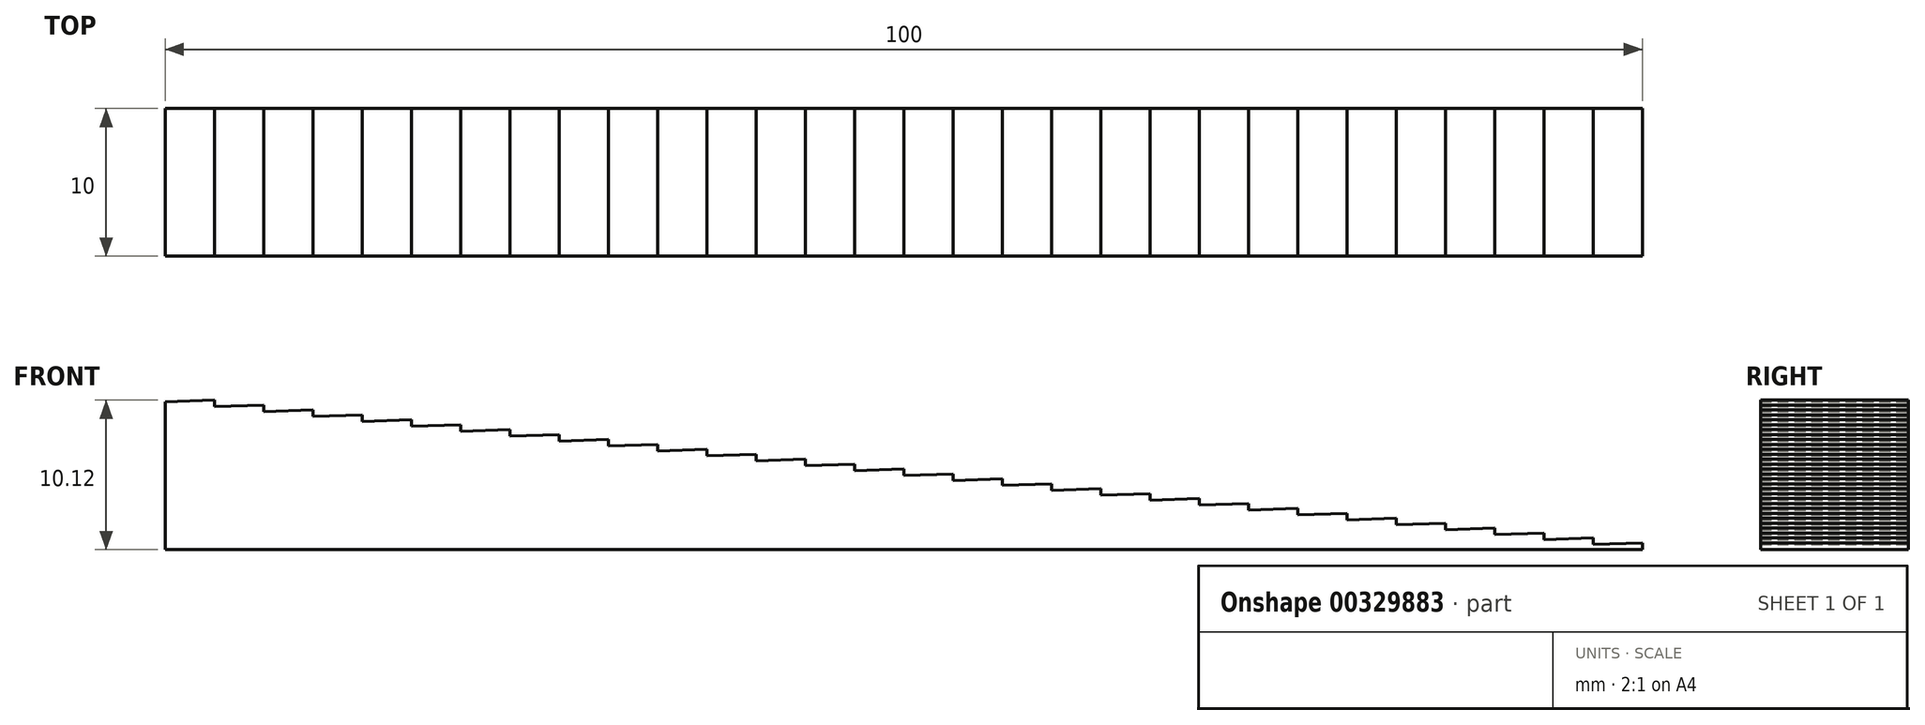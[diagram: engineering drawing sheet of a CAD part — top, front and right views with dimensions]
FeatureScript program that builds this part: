
annotation { "Feature Type Name" : "Feature", "Feature Type Description" : "" }
export const myFeature = defineFeature(function(context is Context, id is Id, definition is map)
    precondition{}
    {
        {
            assignVariable(context, id + "F0", {"variableType" : VariableType.LENGTH, "name" : "Width", "lengthValue" : 10 * mm});
        }
        {
            var Q0;
            Q0=qCreatedBy(makeId("Front.planeOp"),FACE);
            var sketch = newSketch(context, id + "F1", { "sketchPlane" : qUnion([Q0])});
            skLineSegment(sketch, "E0", {"start": v(0, 10) * mm, "end": v(0, 0) * mm});
            skLineSegment(sketch, "E1", {"start": v(0, 0) * mm, "end": v(100, 0) * mm});
            skLineSegment(sketch, "E2", {"start": v(100, 0) * mm, "end": v(100, 0.45) * mm});
            skLineSegment(sketch, "E3", {"start": v(100, 0.45) * mm, "end": v(96.67, 0.33) * mm});
            skLineSegment(sketch, "E4.1.0.0", {"start": v(96.67, 0.78) * mm, "end": v(93.33, 0.67) * mm});
            skLineSegment(sketch, "E4.1.0.1", {"start": v(96.67, 0.33) * mm, "end": v(96.67, 0.78) * mm});
            skLineSegment(sketch, "E4.2.0.0", {"start": v(93.33, 1.12) * mm, "end": v(90, 1) * mm});
            skLineSegment(sketch, "E4.2.0.1", {"start": v(93.33, 0.67) * mm, "end": v(93.33, 1.12) * mm});
            skLineSegment(sketch, "E4.3.0.0", {"start": v(90, 1.45) * mm, "end": v(86.67, 1.33) * mm});
            skLineSegment(sketch, "E4.3.0.1", {"start": v(90, 1) * mm, "end": v(90, 1.45) * mm});
            skLineSegment(sketch, "E4.4.0.0", {"start": v(86.67, 1.78) * mm, "end": v(83.33, 1.67) * mm});
            skLineSegment(sketch, "E4.4.0.1", {"start": v(86.67, 1.33) * mm, "end": v(86.67, 1.78) * mm});
            skLineSegment(sketch, "E4.5.0.0", {"start": v(83.33, 2.12) * mm, "end": v(80, 2) * mm});
            skLineSegment(sketch, "E4.5.0.1", {"start": v(83.33, 1.67) * mm, "end": v(83.33, 2.12) * mm});
            skLineSegment(sketch, "E4.6.0.0", {"start": v(80, 2.45) * mm, "end": v(76.67, 2.33) * mm});
            skLineSegment(sketch, "E4.6.0.1", {"start": v(80, 2) * mm, "end": v(80, 2.45) * mm});
            skLineSegment(sketch, "E4.7.0.0", {"start": v(76.67, 2.78) * mm, "end": v(73.33, 2.67) * mm});
            skLineSegment(sketch, "E4.7.0.1", {"start": v(76.67, 2.33) * mm, "end": v(76.67, 2.78) * mm});
            skLineSegment(sketch, "E4.8.0.0", {"start": v(73.33, 3.12) * mm, "end": v(70, 3) * mm});
            skLineSegment(sketch, "E4.8.0.1", {"start": v(73.33, 2.67) * mm, "end": v(73.33, 3.12) * mm});
            skLineSegment(sketch, "E4.9.0.0", {"start": v(70, 3.45) * mm, "end": v(66.67, 3.33) * mm});
            skLineSegment(sketch, "E4.9.0.1", {"start": v(70, 3) * mm, "end": v(70, 3.45) * mm});
            skLineSegment(sketch, "E4.10.0.0", {"start": v(66.67, 3.78) * mm, "end": v(63.33, 3.67) * mm});
            skLineSegment(sketch, "E4.10.0.1", {"start": v(66.67, 3.33) * mm, "end": v(66.67, 3.78) * mm});
            skLineSegment(sketch, "E4.11.0.0", {"start": v(63.33, 4.12) * mm, "end": v(60, 4) * mm});
            skLineSegment(sketch, "E4.11.0.1", {"start": v(63.33, 3.67) * mm, "end": v(63.33, 4.12) * mm});
            skLineSegment(sketch, "E4.12.0.0", {"start": v(60, 4.45) * mm, "end": v(56.67, 4.33) * mm});
            skLineSegment(sketch, "E4.12.0.1", {"start": v(60, 4) * mm, "end": v(60, 4.45) * mm});
            skLineSegment(sketch, "E4.13.0.0", {"start": v(56.67, 4.78) * mm, "end": v(53.33, 4.67) * mm});
            skLineSegment(sketch, "E4.13.0.1", {"start": v(56.67, 4.33) * mm, "end": v(56.67, 4.78) * mm});
            skLineSegment(sketch, "E4.14.0.0", {"start": v(53.33, 5.12) * mm, "end": v(50, 5) * mm});
            skLineSegment(sketch, "E4.14.0.1", {"start": v(53.33, 4.67) * mm, "end": v(53.33, 5.12) * mm});
            skLineSegment(sketch, "E4.15.0.0", {"start": v(50, 5.45) * mm, "end": v(46.67, 5.33) * mm});
            skLineSegment(sketch, "E4.15.0.1", {"start": v(50, 5) * mm, "end": v(50, 5.45) * mm});
            skLineSegment(sketch, "E4.16.0.0", {"start": v(46.67, 5.78) * mm, "end": v(43.33, 5.67) * mm});
            skLineSegment(sketch, "E4.16.0.1", {"start": v(46.67, 5.33) * mm, "end": v(46.67, 5.78) * mm});
            skLineSegment(sketch, "E4.17.0.0", {"start": v(43.33, 6.12) * mm, "end": v(40, 6) * mm});
            skLineSegment(sketch, "E4.17.0.1", {"start": v(43.33, 5.67) * mm, "end": v(43.33, 6.12) * mm});
            skLineSegment(sketch, "E4.18.0.0", {"start": v(40, 6.45) * mm, "end": v(36.67, 6.33) * mm});
            skLineSegment(sketch, "E4.18.0.1", {"start": v(40, 6) * mm, "end": v(40, 6.45) * mm});
            skLineSegment(sketch, "E4.19.0.0", {"start": v(36.67, 6.78) * mm, "end": v(33.33, 6.67) * mm});
            skLineSegment(sketch, "E4.19.0.1", {"start": v(36.67, 6.33) * mm, "end": v(36.67, 6.78) * mm});
            skLineSegment(sketch, "E4.20.0.0", {"start": v(33.33, 7.12) * mm, "end": v(30, 7) * mm});
            skLineSegment(sketch, "E4.20.0.1", {"start": v(33.33, 6.67) * mm, "end": v(33.33, 7.12) * mm});
            skLineSegment(sketch, "E4.21.0.0", {"start": v(30, 7.45) * mm, "end": v(26.67, 7.33) * mm});
            skLineSegment(sketch, "E4.21.0.1", {"start": v(30, 7) * mm, "end": v(30, 7.45) * mm});
            skLineSegment(sketch, "E4.22.0.0", {"start": v(26.67, 7.78) * mm, "end": v(23.33, 7.67) * mm});
            skLineSegment(sketch, "E4.22.0.1", {"start": v(26.67, 7.33) * mm, "end": v(26.67, 7.78) * mm});
            skLineSegment(sketch, "E4.23.0.0", {"start": v(23.33, 8.12) * mm, "end": v(20, 8) * mm});
            skLineSegment(sketch, "E4.23.0.1", {"start": v(23.33, 7.67) * mm, "end": v(23.33, 8.12) * mm});
            skLineSegment(sketch, "E4.24.0.0", {"start": v(20, 8.45) * mm, "end": v(16.67, 8.33) * mm});
            skLineSegment(sketch, "E4.24.0.1", {"start": v(20, 8) * mm, "end": v(20, 8.45) * mm});
            skLineSegment(sketch, "E4.25.0.0", {"start": v(16.67, 8.78) * mm, "end": v(13.33, 8.67) * mm});
            skLineSegment(sketch, "E4.25.0.1", {"start": v(16.67, 8.33) * mm, "end": v(16.67, 8.78) * mm});
            skLineSegment(sketch, "E4.26.0.0", {"start": v(13.33, 9.12) * mm, "end": v(10, 9) * mm});
            skLineSegment(sketch, "E4.26.0.1", {"start": v(13.33, 8.67) * mm, "end": v(13.33, 9.12) * mm});
            skLineSegment(sketch, "E4.27.0.0", {"start": v(10, 9.45) * mm, "end": v(6.67, 9.33) * mm});
            skLineSegment(sketch, "E4.27.0.1", {"start": v(10, 9) * mm, "end": v(10, 9.45) * mm});
            skLineSegment(sketch, "E4.28.0.0", {"start": v(6.67, 9.78) * mm, "end": v(3.33, 9.67) * mm});
            skLineSegment(sketch, "E4.28.0.1", {"start": v(6.67, 9.33) * mm, "end": v(6.67, 9.78) * mm});
            skLineSegment(sketch, "E4.29.0.0", {"start": v(3.33, 10.12) * mm, "end": v(0, 10) * mm});
            skLineSegment(sketch, "E4.29.0.1", {"start": v(3.33, 9.67) * mm, "end": v(3.33, 10.12) * mm});
            skLineSegment(sketch, "E4.direction1", {"start": v(96.67, 0.33) * mm, "end": v(93.33, 0.67) * mm, "construction": true});
            skLineSegment(sketch, "E5", {"start": v(100, 10) * mm, "end": v(0, 10) * mm, "construction": true});
            skSolve(sketch);
        }
        {
            var Q0;
            Q0 = qSketchRegion(id + "F1", true);
            extrude(context, id + "F2", {"entities" : qUnion([Q0]), "depth" : getVariable(context, 'Width'), "offsetDistance" : 25 * mm});
        }
    });
